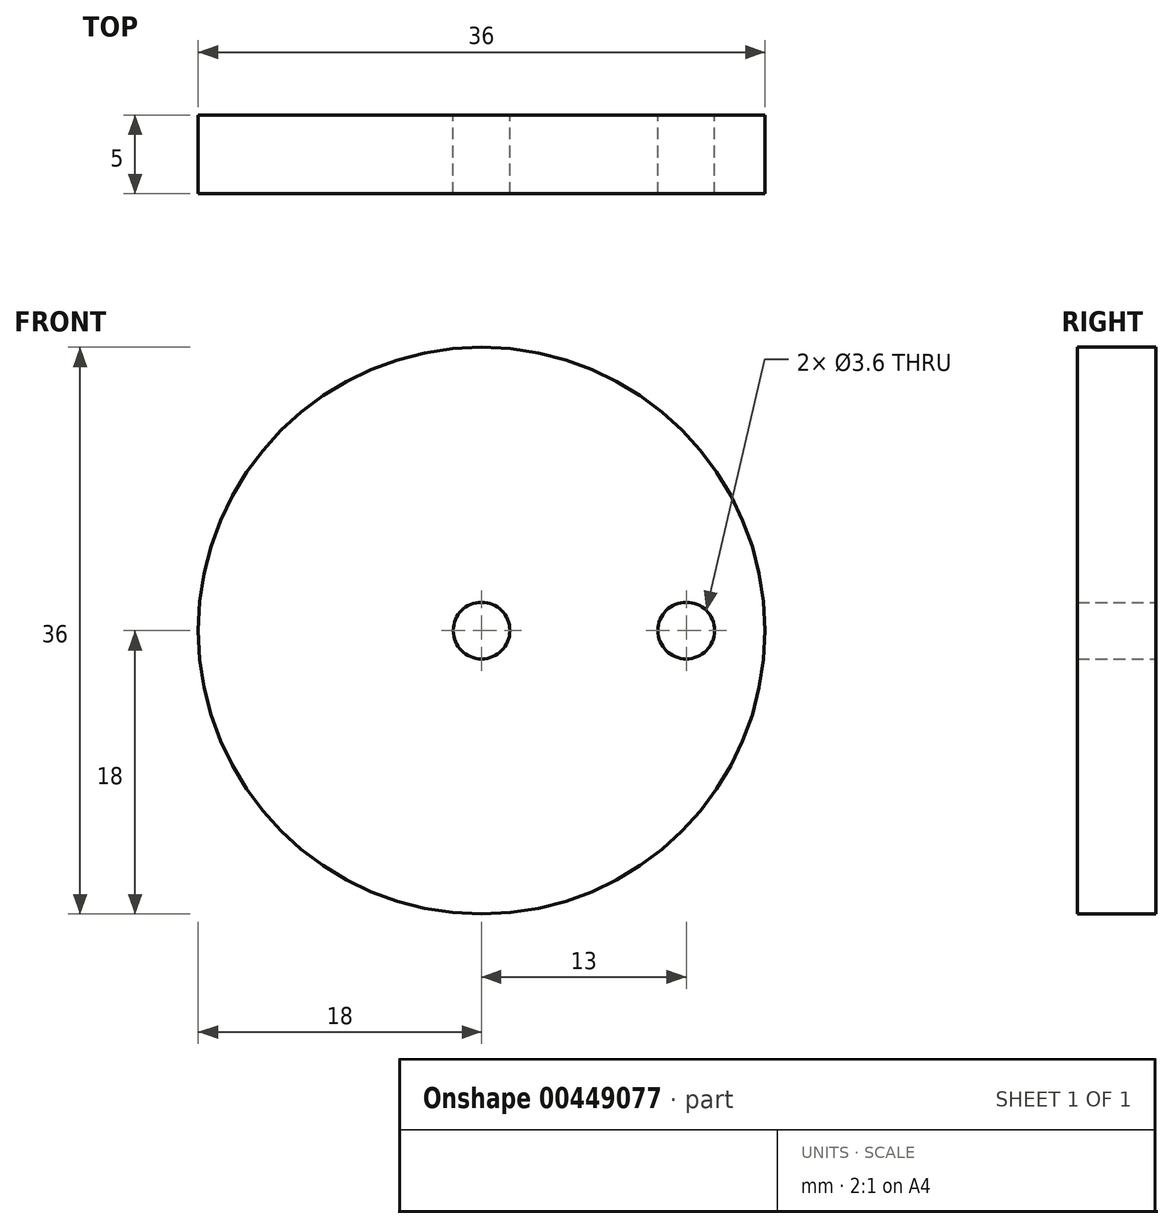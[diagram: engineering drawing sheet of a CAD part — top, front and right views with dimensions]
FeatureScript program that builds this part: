
annotation { "Feature Type Name" : "Feature", "Feature Type Description" : "" }
export const myFeature = defineFeature(function(context is Context, id is Id, definition is map)
    precondition{}
    {
        {
            var Q0;
            Q0=qCreatedBy(makeId("Front.planeOp"),FACE);
            var sketch = newSketch(context, id + "F0", { "sketchPlane" : qUnion([Q0])});
            skCircle(sketch, "E0", {"center": v(0, 0) * mm, "radius": 18 * mm});
            skCircle(sketch, "E1", {"center": v(13, 0) * mm, "radius": 1.8 * mm});
            skCircle(sketch, "E2", {"center": v(0, 0) * mm, "radius": 1.8 * mm});
            skSolve(sketch);
        }
        {
            var Q0;
            Q0=makeQuery(id+"F0.imprint","IMPRINT",FACE,{"disambiguationData":[TD([[makeQuery(id+"F0.imprint","IMPRINT",EDGE,{"derivedFrom":sQuery(id+"F0.wireOp",EDGE,"E0")}),1.0]])]});
            extrude(context, id + "F1", {"entities" : qUnion([Q0]), "depth" : 5 * mm});
        }
    });
